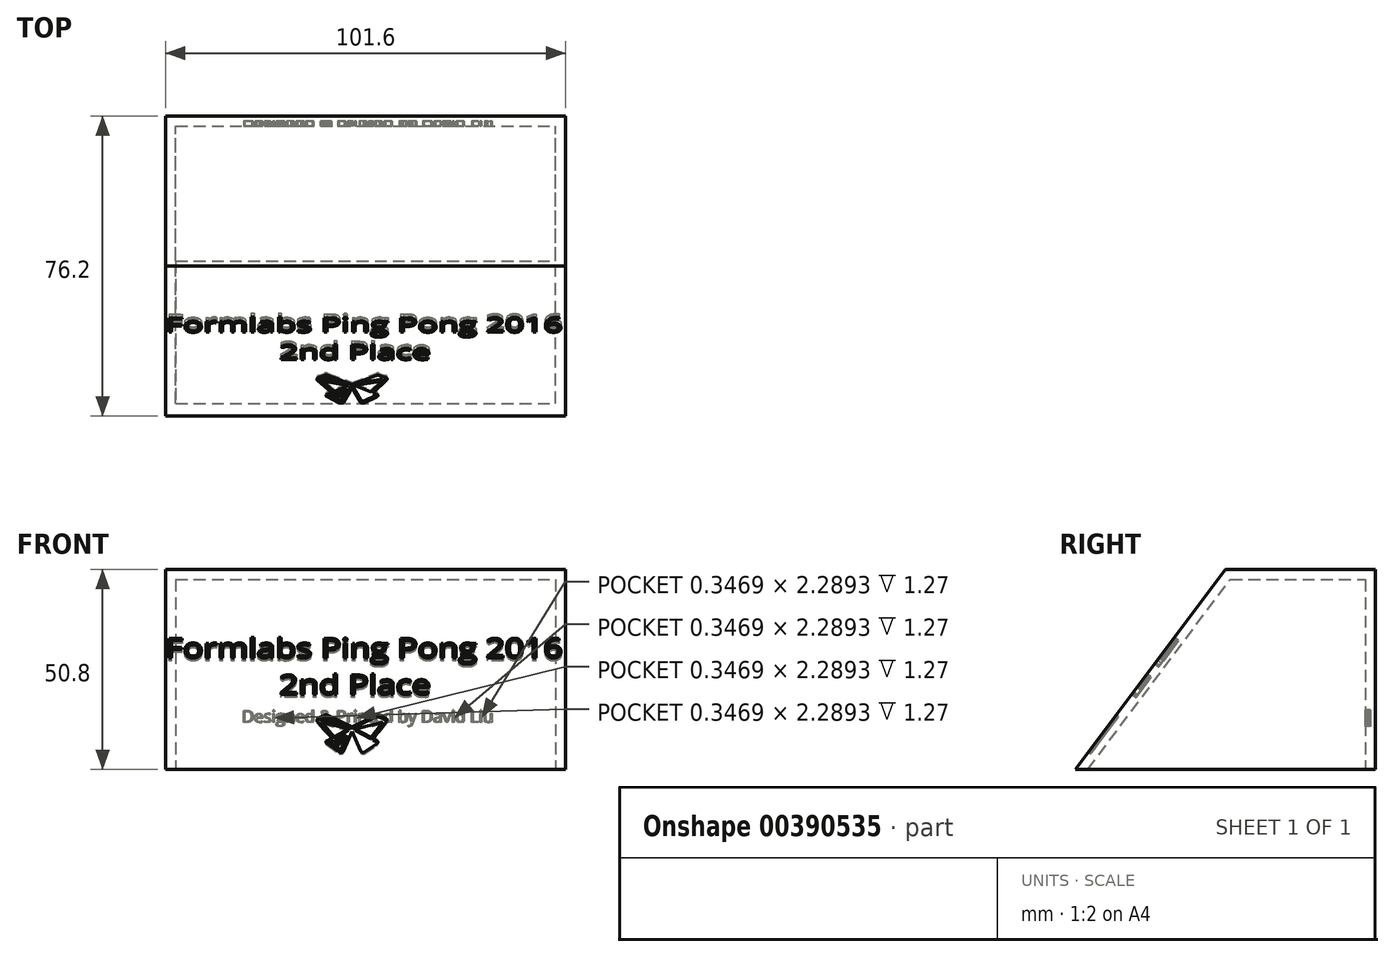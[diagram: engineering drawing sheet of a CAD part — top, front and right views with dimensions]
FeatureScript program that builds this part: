
annotation { "Feature Type Name" : "Feature", "Feature Type Description" : "" }
export const myFeature = defineFeature(function(context is Context, id is Id, definition is map)
    precondition{}
    {
        {
            var Q0;
            Q0=qCreatedBy(makeId("Top.planeOp"),FACE);
            var sketch = newSketch(context, id + "F0", { "sketchPlane" : qUnion([Q0])});
            skLineSegment(sketch, "E0.bottom", {"start": v(-33.87, 0) * mm, "end": v(67.73, 0) * mm});
            skLineSegment(sketch, "E0.top", {"start": v(-33.87, 76.2) * mm, "end": v(67.73, 76.2) * mm});
            skLineSegment(sketch, "E0.left", {"start": v(-33.87, 0) * mm, "end": v(-33.87, 76.2) * mm});
            skLineSegment(sketch, "E0.right", {"start": v(67.73, 0) * mm, "end": v(67.73, 76.2) * mm});
            skSolve(sketch);
        }
        {
            var Q0;
            Q0=makeQuery(id+"F0.imprint","IMPRINT",FACE,{"disambiguationData":[TD([[makeQuery(id+"F0.imprint","IMPRINT",EDGE,{"derivedFrom":sQuery(id+"F0.wireOp",EDGE,"E0.bottom")}),1.0]])]});
            extrude(context, id + "F1", {"entities" : qUnion([Q0]), "depth" : 50.8 * mm});
        }
        {
            var Q0;
            Q0=makeQuery(id+"F1.opExtrude","SWEPT_FACE",FACE,{"disambiguationData":[OSD([sQuery(id+"F0.wireOp",EDGE,"E0.right")])]});
            var sketch = newSketch(context, id + "F2", { "sketchPlane" : qUnion([Q0])});
            skLineSegment(sketch, "E1", {"start": v(0, 0) * mm, "end": v(38.1, 50.8) * mm});
            skLineSegment(sketch, "E2", {"start": v(38.1, 50.8) * mm, "end": v(0, 50.8) * mm});
            skLineSegment(sketch, "E3", {"start": v(0, 50.8) * mm, "end": v(0, 0) * mm});
            skSolve(sketch);
        }
        {
            var Q0;
            Q0=makeQuery(id+"F2.imprint","IMPRINT",FACE,{"disambiguationData":[TD([[makeQuery(id+"F2.imprint","IMPRINT",EDGE,{"derivedFrom":sQuery(id+"F2.wireOp",EDGE,"E1")}),1.0]])]});
            extrude(context, id + "F3", {"entities" : qUnion([Q0]), "operationType" : NewBodyOperationType.REMOVE, "endBound" : BoundingType.THROUGH_ALL, "oppositeDirection" : true, "depth" : 25.4 * mm});
        }
        {
            var Q0;
            Q0=makeQuery(id+"F1.opExtrude","CAP_FACE",FACE,{"disambiguationData":[OSD([sQuery(id+"F0.wireOp",EDGE,"E0.bottom"),sQuery(id+"F0.wireOp",EDGE,"E0.top"),sQuery(id+"F0.wireOp",EDGE,"E0.left"),sQuery(id+"F0.wireOp",EDGE,"E0.right")])],"isStart":true});
            shell(context, id + "F4", {"entities" : qUnion([Q0]), "thickness" : 2.54 * mm});
        }
        {
            var Q0;
            Q0=makeQuery(id+"F3.boolean.opBoolean","COPY",FACE,{"derivedFrom":makeQuery(id+"F3.opExtrude","SWEPT_FACE",FACE,{"disambiguationData":[OSD([sQuery(id+"F2.wireOp",EDGE,"E1")])]})});
            var sketch = newSketch(context, id + "F5", { "sketchPlane" : qUnion([Q0])});
            skText(sketch, "E4", { "text": "Formlabs Ping Pong 2016\n             2nd Place", "fontName": "OpenSans-Regular.ttf"});
            const initialGuessF5  = {"E4": [-0.03388, 0.03549, 1, 0, 0.00615]};
            skSetInitialGuess(sketch, initialGuessF5);
            skSolve(sketch);
        }
        {
            var Q0;
            Q0=qSketchRegion(id+"F5",true);
            extrude(context, id + "F6", {"entities" : qUnion([Q0]), "operationType" : NewBodyOperationType.REMOVE, "oppositeDirection" : true, "depth" : 1.27 * mm});
        }
        {
            var Q0;
            {var subQ1=sQuery(id+"F0.wireOp",EDGE,"E0.left");Q0=makeQuery(id+"F6.boolean.opBoolean","SPLIT",FACE,{"disambiguationData":[TD([makeQuery(id+"F1.opExtrude","SWEPT_FACE",FACE,{"disambiguationData":[OSD([subQ1])]})])],"derivedFrom":makeQuery(id+"F3.boolean.opBoolean","COPY",FACE,{"derivedFrom":makeQuery(id+"F3.opExtrude","SWEPT_FACE",FACE,{"disambiguationData":[OSD([sQuery(id+"F2.wireOp",EDGE,"E1")])]})})});}
            var sketch = newSketch(context, id + "F7", { "sketchPlane" : qUnion([Q0])});
            skLineSegment(sketch, "E5", {"start": v(7.36, 17.12) * mm, "end": v(13.48, 13.43) * mm});
            skLineSegment(sketch, "E6", {"start": v(13.48, 13.43) * mm, "end": v(19.63, 17.12) * mm});
            skLineSegment(sketch, "E7", {"start": v(21.3, 14.9) * mm, "end": v(14.26, 12.82) * mm});
            skLineSegment(sketch, "E8", {"start": v(14.26, 12.82) * mm, "end": v(18.27, 10.15) * mm});
            skLineSegment(sketch, "E9", {"start": v(18.27, 10.15) * mm, "end": v(21.3, 14.9) * mm});
            skLineSegment(sketch, "E10", {"start": v(22.26, 15.24) * mm, "end": v(18.81, 9.77) * mm});
            skLineSegment(sketch, "E11", {"start": v(18.81, 9.77) * mm, "end": v(19.74, 9.2) * mm});
            skLineSegment(sketch, "E12", {"start": v(12.62, 12.84) * mm, "end": v(8.98, 10.35) * mm});
            skLineSegment(sketch, "E13", {"start": v(8.98, 10.35) * mm, "end": v(5.87, 14.9) * mm});
            skLineSegment(sketch, "E14", {"start": v(5.87, 14.9) * mm, "end": v(12.62, 12.84) * mm});
            skLineSegment(sketch, "E15", {"start": v(11.48, 11.05) * mm, "end": v(9.95, 8.92) * mm});
            skLineSegment(sketch, "E16", {"start": v(9.95, 8.92) * mm, "end": v(9.46, 9.61) * mm});
            skLineSegment(sketch, "E17", {"start": v(9.46, 9.61) * mm, "end": v(11.48, 11.05) * mm});
            skLineSegment(sketch, "E18", {"start": v(12.25, 10.8) * mm, "end": v(10.73, 6.26) * mm});
            skLineSegment(sketch, "E19", {"start": v(10.73, 6.26) * mm, "end": v(7.92, 8.58) * mm});
            skLineSegment(sketch, "E20", {"start": v(7.92, 8.58) * mm, "end": v(8.75, 9.23) * mm});
            skLineSegment(sketch, "E21", {"start": v(7.06, 16.43) * mm, "end": v(10.55, 14.3) * mm});
            skLineSegment(sketch, "E22", {"start": v(10.55, 14.3) * mm, "end": v(5.8, 15.73) * mm});
            skLineSegment(sketch, "E23", {"start": v(5.8, 15.73) * mm, "end": v(7.06, 16.43) * mm});
            skLineSegment(sketch, "E24", {"start": v(13.5, 12.14) * mm, "end": v(15.58, 5.93) * mm});
            skLineSegment(sketch, "E25", {"start": v(13.5, 12.14) * mm, "end": v(11.34, 5.9) * mm});
            skLineSegment(sketch, "E26", {"start": v(7.14, 8.19) * mm, "end": v(10.22, 5.56) * mm});
            skLineSegment(sketch, "E27", {"start": v(8.25, 9.94) * mm, "end": v(7.08, 9.13) * mm});
            skLineSegment(sketch, "E28", {"start": v(5.04, 16.35) * mm, "end": v(6.52, 17.23) * mm});
            skLineSegment(sketch, "E29", {"start": v(20.34, 17.22) * mm, "end": v(22.03, 16.28) * mm});
            skLineSegment(sketch, "E30", {"start": v(16.53, 5.46) * mm, "end": v(19.73, 8.08) * mm});
            skLineSegment(sketch, "E31", {"start": v(12.25, 10.8) * mm, "end": v(10.27, 8.05) * mm});
            skArc(sketch, "E32", {"start": v(5.04, 16.35) * mm, "mid": v(4.6, 15.76) * mm, "end": v(4.7, 15.02) * mm});
            skArc(sketch, "E33", {"start": v(6.52, 17.23) * mm, "mid": v(6.96, 17.32) * mm, "end": v(7.36, 17.12) * mm});
            skArc(sketch, "E34", {"start": v(7.08, 9.13) * mm, "mid": v(6.85, 8.65) * mm, "end": v(7.14, 8.19) * mm});
            skArc(sketch, "E35", {"start": v(11.34, 5.9) * mm, "mid": v(10.87, 5.44) * mm, "end": v(10.22, 5.56) * mm});
            skArc(sketch, "E36", {"start": v(15.58, 5.93) * mm, "mid": v(15.96, 5.5) * mm, "end": v(16.53, 5.46) * mm});
            skArc(sketch, "E37", {"start": v(19.74, 9.2) * mm, "mid": v(20.04, 8.64) * mm, "end": v(19.73, 8.08) * mm});
            skArc(sketch, "E38", {"start": v(22.03, 16.28) * mm, "mid": v(22.38, 15.81) * mm, "end": v(22.26, 15.24) * mm});
            skArc(sketch, "E39", {"start": v(20.34, 17.22) * mm, "mid": v(19.97, 17.29) * mm, "end": v(19.63, 17.12) * mm});
            skArc(sketch, "E40", {"start": v(9.43, 8.25) * mm, "mid": v(9.8, 8) * mm, "end": v(10.27, 8.05) * mm});
            skLineSegment(sketch, "E41", {"start": v(4.7, 15.02) * mm, "end": v(8.25, 9.94) * mm});
            skLineSegment(sketch, "E42", {"start": v(8.75, 9.23) * mm, "end": v(9.43, 8.25) * mm});
            skSolve(sketch);
        }
        {
            var Q0;
            Q0=makeQuery(id+"F7.imprint","IMPRINT",FACE,{"disambiguationData":[TD([[makeQuery(id+"F7.imprint","IMPRINT",EDGE,{"derivedFrom":sQuery(id+"F7.wireOp",EDGE,"E5")}),-1.0]])]});
            extrude(context, id + "F8", {"entities" : qUnion([Q0]), "operationType" : NewBodyOperationType.REMOVE, "oppositeDirection" : true, "depth" : 0.64 * mm});
        }
        {
            var Q0;
            Q0=makeQuery(id+"F4.opShell","OFFSET_FACE",FACE,{"disambiguationData":[OSD([sQuery(id+"F0.wireOp",EDGE,"E0.top")])]});
            var sketch = newSketch(context, id + "F9", { "sketchPlane" : qUnion([Q0])});
            skText(sketch, "E43", { "text": "Designed & Printed by David Liu", "fontName": "OpenSans-Regular.ttf"});
            const initialGuessF9  = {"E43": [-0.01454, 0.01193, 1, 0, 0.00308]};
            skSetInitialGuess(sketch, initialGuessF9);
            skSolve(sketch);
        }
        {
            var Q0;
            Q0 = qSketchRegion(id + "F9", true);
            extrude(context, id + "F10", {"entities" : qUnion([Q0]), "operationType" : NewBodyOperationType.REMOVE, "oppositeDirection" : true, "depth" : 1.27 * mm});
        }
    });
